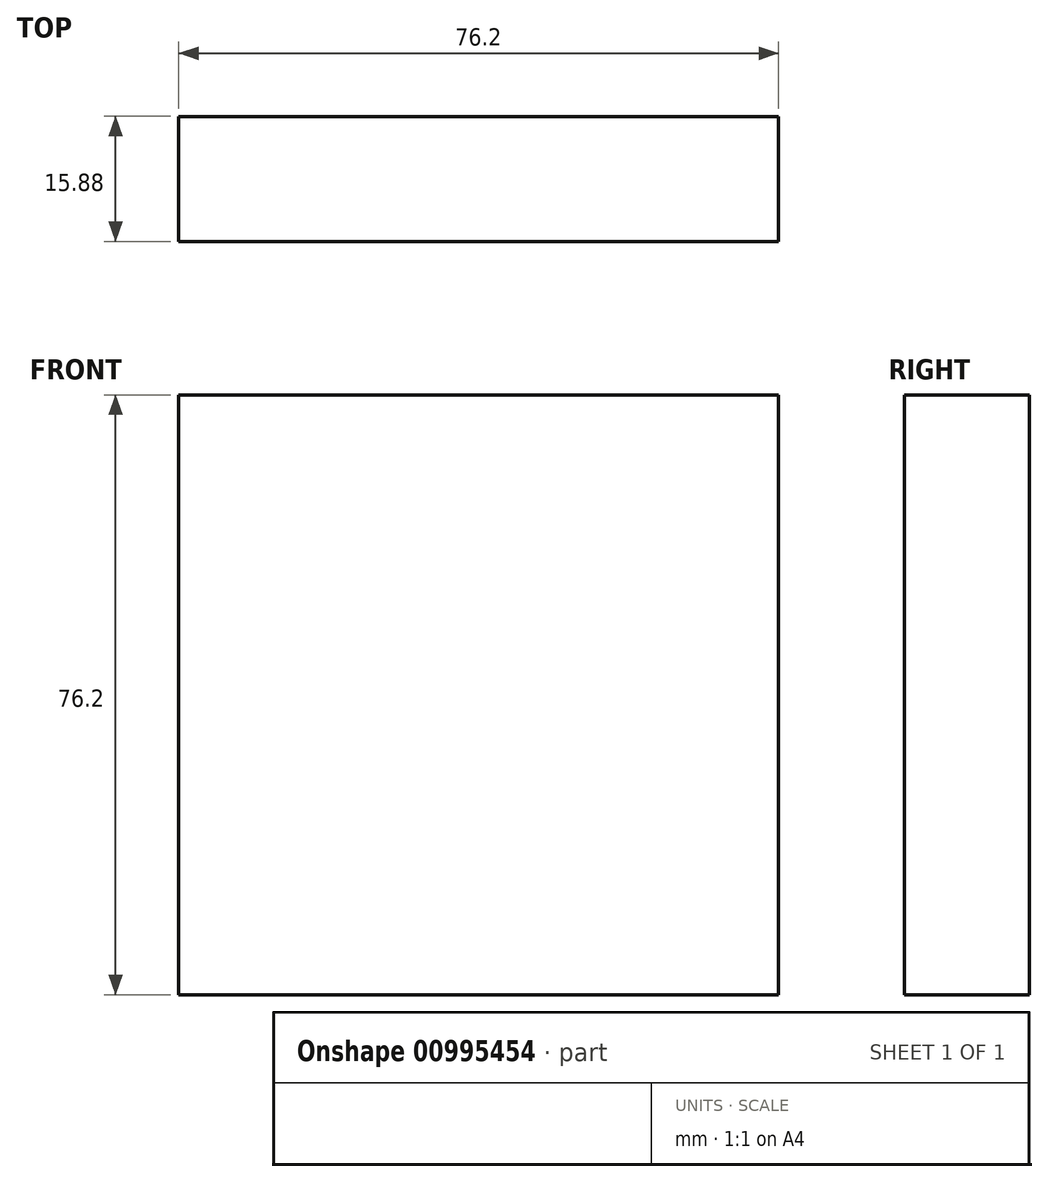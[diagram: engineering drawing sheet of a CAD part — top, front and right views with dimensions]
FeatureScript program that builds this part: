
annotation { "Feature Type Name" : "Feature", "Feature Type Description" : "" }
export const myFeature = defineFeature(function(context is Context, id is Id, definition is map)
    precondition{}
    {
        {
            var Q0;
            Q0=qCreatedBy(makeId("Front.planeOp"),FACE);
            var sketch = newSketch(context, id + "F0", { "sketchPlane" : qUnion([Q0])});
            skLineSegment(sketch, "E0.bottom", {"start": v(0, 0) * mm, "end": v(76.2, 0) * mm});
            skLineSegment(sketch, "E0.top", {"start": v(0, 76.2) * mm, "end": v(76.2, 76.2) * mm});
            skLineSegment(sketch, "E0.left", {"start": v(0, 0) * mm, "end": v(0, 76.2) * mm});
            skLineSegment(sketch, "E0.right", {"start": v(76.2, 0) * mm, "end": v(76.2, 76.2) * mm});
            skSolve(sketch);
        }
        {
            var Q0;
            Q0=makeQuery(id+"F0.imprint","IMPRINT",FACE,{"disambiguationData":[TD([[makeQuery(id+"F0.imprint","IMPRINT",EDGE,{"derivedFrom":sQuery(id+"F0.wireOp",EDGE,"E0.bottom")}),1.0]])]});
            extrude(context, id + "F1", {"entities" : qUnion([Q0]), "oppositeDirection" : true, "depth" : 15.88 * mm, "offsetDistance" : 25.4 * mm});
        }
    });
